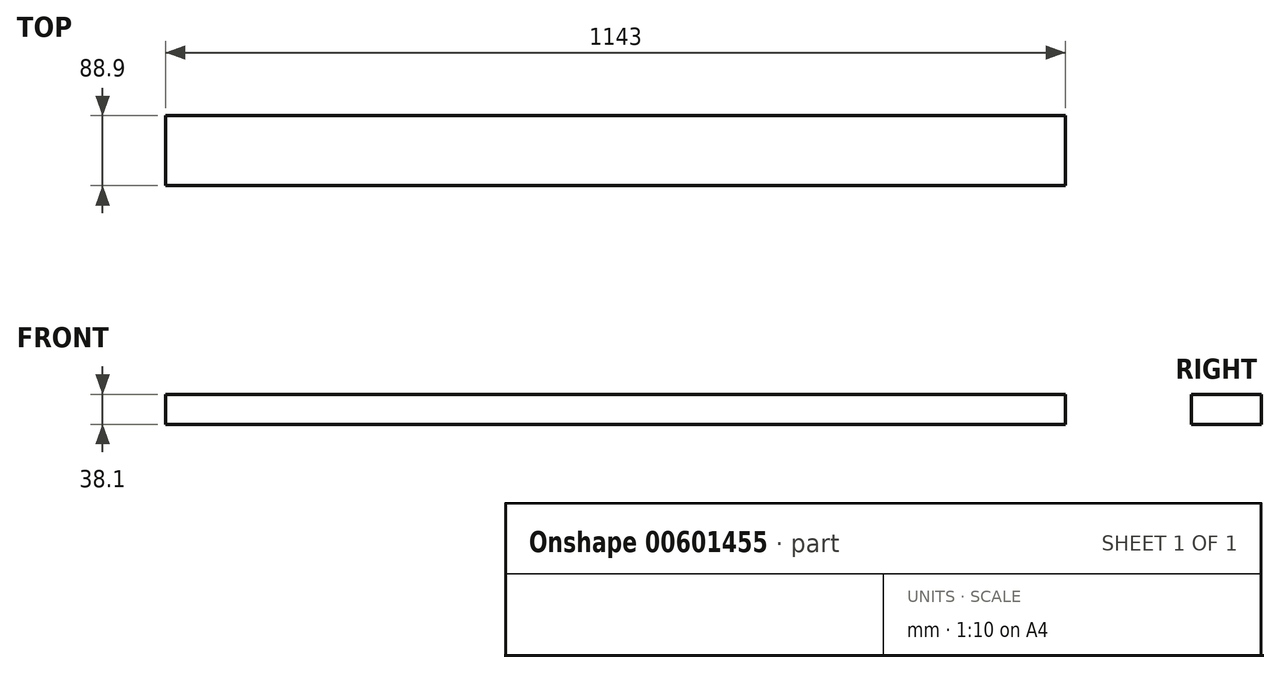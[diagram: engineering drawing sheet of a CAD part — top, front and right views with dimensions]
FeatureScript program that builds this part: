
annotation { "Feature Type Name" : "Feature", "Feature Type Description" : "" }
export const myFeature = defineFeature(function(context is Context, id is Id, definition is map)
    precondition{}
    {
        {
            var Q0;
            Q0=qCreatedBy(makeId("Top.planeOp"),FACE);
            var sketch = newSketch(context, id + "F0", { "sketchPlane" : qUnion([Q0])});
            skLineSegment(sketch, "E0.bottom", {"start": v(0, 0) * mm, "end": v(1143, 0) * mm});
            skLineSegment(sketch, "E0.top", {"start": v(0, 88.9) * mm, "end": v(1143, 88.9) * mm});
            skLineSegment(sketch, "E0.left", {"start": v(0, 0) * mm, "end": v(0, 88.9) * mm});
            skLineSegment(sketch, "E0.right", {"start": v(1143, 0) * mm, "end": v(1143, 88.9) * mm});
            skSolve(sketch);
        }
        {
            var Q0;
            Q0=qSketchRegion(id+"F0",true);
            extrude(context, id + "F1", {"entities" : qUnion([Q0]), "depth" : 38.1 * mm, "offsetDistance" : 25.4 * mm});
        }
    });
